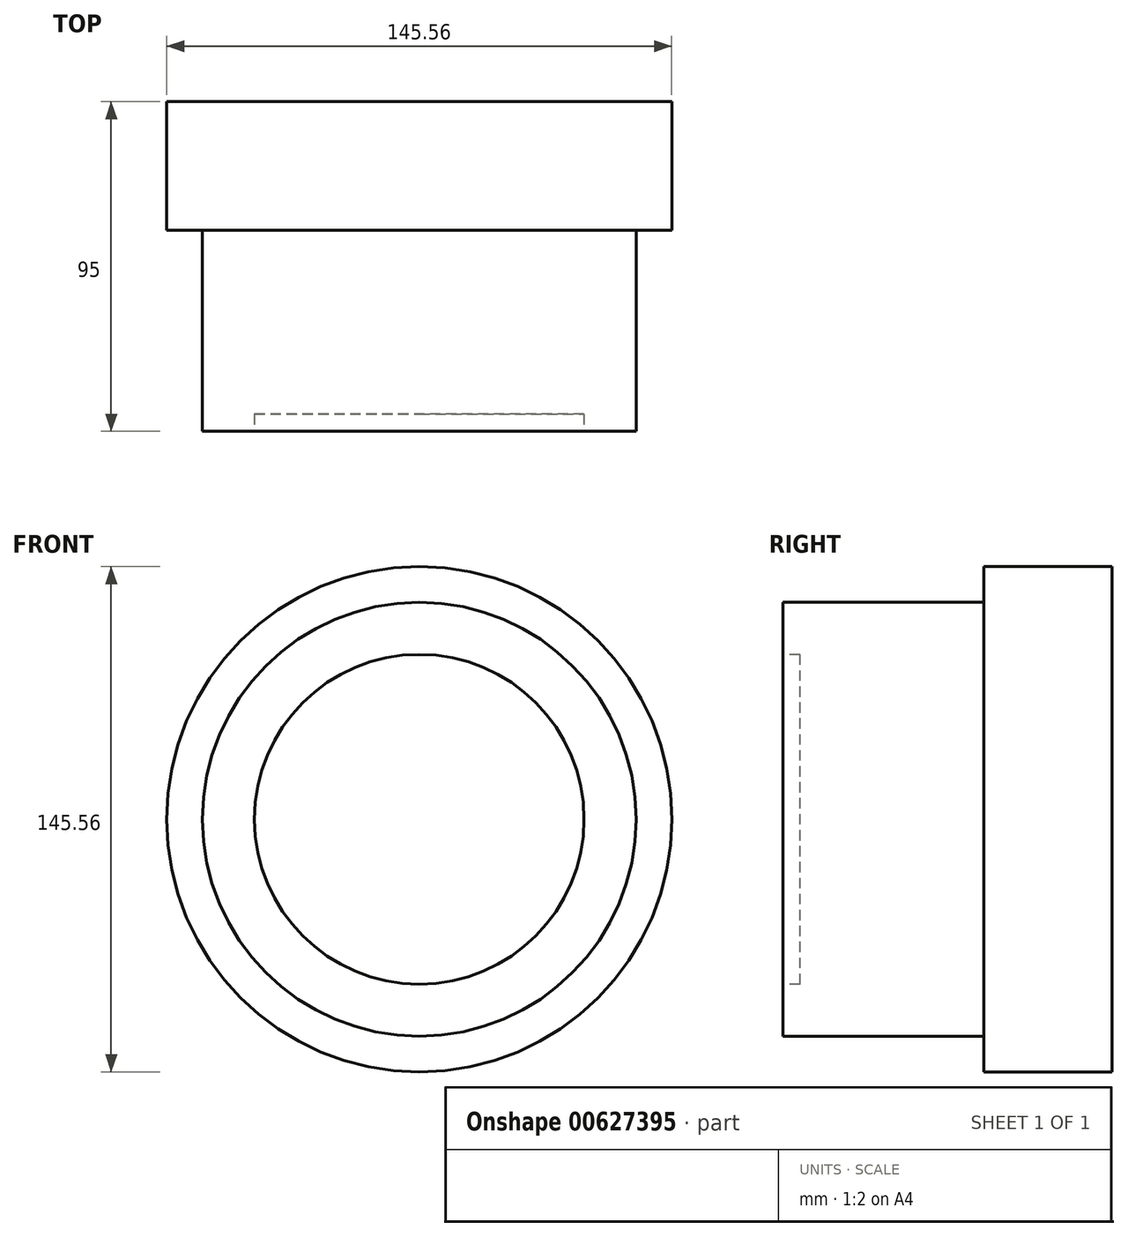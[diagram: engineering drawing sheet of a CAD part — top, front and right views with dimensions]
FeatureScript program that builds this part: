
annotation { "Feature Type Name" : "Feature", "Feature Type Description" : "" }
export const myFeature = defineFeature(function(context is Context, id is Id, definition is map)
    precondition{}
    {
        {
            var Q0;
            Q0=qCreatedBy(makeId("Right.planeOp"),FACE);
            var sketch = newSketch(context, id + "F0", { "sketchPlane" : qUnion([Q0])});
            skLineSegment(sketch, "E0.bottom", {"start": v(5, 0) * mm, "end": v(57.94, 0) * mm});
            skLineSegment(sketch, "E0.top", {"start": v(0, 62.5) * mm, "end": v(57.94, 62.5) * mm});
            skLineSegment(sketch, "E0.left", {"start": v(0, 47.5) * mm, "end": v(0, 62.5) * mm});
            skLineSegment(sketch, "E0.right", {"start": v(57.94, 0) * mm, "end": v(57.94, 62.5) * mm});
            skLineSegment(sketch, "E1.bottom", {"start": v(57.94, 0) * mm, "end": v(95, 0) * mm});
            skLineSegment(sketch, "E1.top", {"start": v(57.94, 72.78) * mm, "end": v(95, 72.78) * mm});
            skLineSegment(sketch, "E1.left", {"start": v(57.94, 0) * mm, "end": v(57.94, 72.78) * mm});
            skLineSegment(sketch, "E1.right", {"start": v(95, 0) * mm, "end": v(95, 72.78) * mm});
            skLineSegment(sketch, "E2.top", {"start": v(0, 47.5) * mm, "end": v(5, 47.5) * mm});
            skLineSegment(sketch, "E2.right", {"start": v(5, 0) * mm, "end": v(5, 47.5) * mm});
            skSolve(sketch);
        }
        {
            var Q0;
            Q0=qCreatedBy(makeId("Right.planeOp"),FACE);
            var sketch = newSketch(context, id + "F1", { "sketchPlane" : qUnion([Q0])});
            skLineSegment(sketch, "E3", {"start": v(-61.75, 0) * mm, "end": v(132.79, 0) * mm, "construction": true});
            skSolve(sketch);
        }
        {
            var Q0;
            {var subQ2=sQuery(id+"F0.wireOp",EDGE,"E0.bottom");Q0=makeQuery(id+"F0.imprint","IMPRINT",FACE,{"disambiguationData":[TD([[makeQuery(id+"F0.imprint","IMPRINT",EDGE,{"derivedFrom":subQ2}),1.0]])]});}
            var Q1;
            {var subQ3=sQuery(id+"F0.wireOp",EDGE,"E1.bottom");Q1=makeQuery(id+"F0.imprint","IMPRINT",FACE,{"disambiguationData":[TD([[makeQuery(id+"F0.imprint","IMPRINT",EDGE,{"derivedFrom":subQ3}),1.0]])]});}
            var Q2;
            Q2=sQuery(id+"F1.wireOp",EDGE,"E3");
            revolve(context, id + "F2", {"entities" : qUnion([Q0, Q1]), "axis" : qUnion([Q2]), "revolveType" : RevolveType.FULL});
        }
    });
